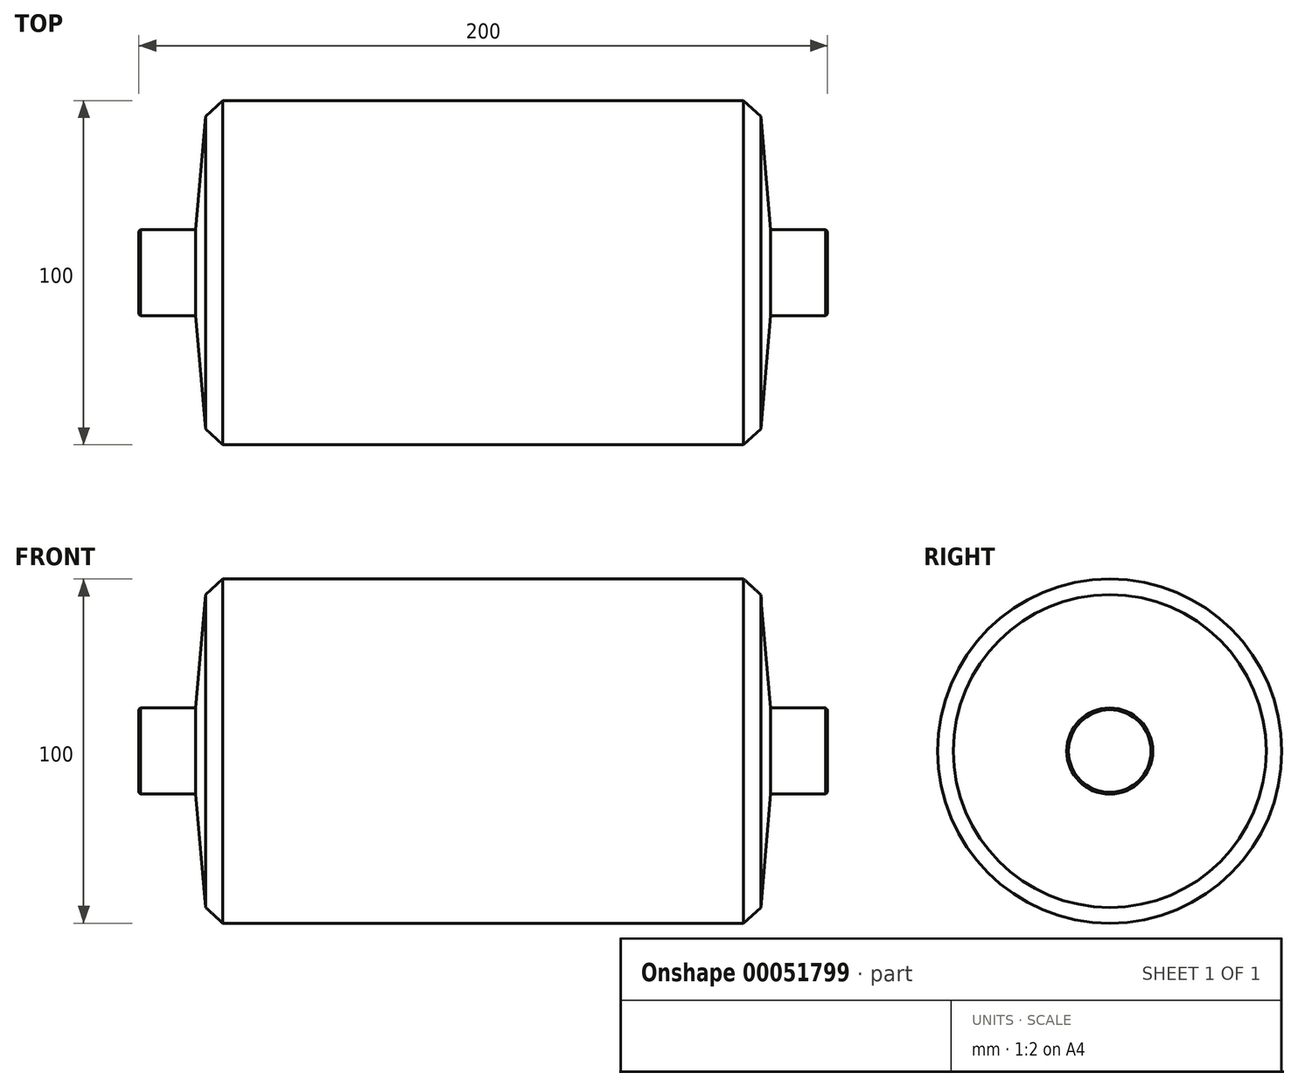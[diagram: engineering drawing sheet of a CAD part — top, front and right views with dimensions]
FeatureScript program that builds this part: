
annotation { "Feature Type Name" : "Feature", "Feature Type Description" : "" }
export const myFeature = defineFeature(function(context is Context, id is Id, definition is map)
    precondition{}
    {
        {
            var Q0;
            Q0=qCreatedBy(makeId("Top.planeOp"),FACE);
            var sketch = newSketch(context, id + "F0", { "sketchPlane" : qUnion([Q0])});
            skLineSegment(sketch, "E0", {"start": v(0, 0) * mm, "end": v(200, 0) * mm});
            skLineSegment(sketch, "E1", {"start": v(200, 0) * mm, "end": v(200, 12.5) * mm});
            skLineSegment(sketch, "E2", {"start": v(200, 12.5) * mm, "end": v(183.5, 12.5) * mm});
            skLineSegment(sketch, "E3", {"start": v(183.5, 12.5) * mm, "end": v(180.22, 50) * mm});
            skLineSegment(sketch, "E4", {"start": v(19.78, 50) * mm, "end": v(16.5, 12.5) * mm});
            skLineSegment(sketch, "E5", {"start": v(16.5, 12.5) * mm, "end": v(0, 12.5) * mm});
            skLineSegment(sketch, "E6", {"start": v(0, 12.5) * mm, "end": v(0, 0) * mm});
            skLineSegment(sketch, "E7", {"start": v(19.78, 50) * mm, "end": v(180.22, 50) * mm});
            skSolve(sketch);
        }
        {
            var Q0;
            Q0=makeQuery(id+"F0.imprint","IMPRINT",FACE,{"disambiguationData":[TD([[makeQuery(id+"F0.imprint","IMPRINT",EDGE,{"derivedFrom":sQuery(id+"F0.wireOp",EDGE,"E0")}),1.0]])]});
            var Q1;
            Q1=sQuery(id+"F0.wireOp",EDGE,"E0");
            revolve(context, id + "F1", {"entities" : qUnion([Q0]), "axis" : qUnion([Q1]), "revolveType" : RevolveType.FULL});
        }
        {
            var Q0;
            Q0=makeQuery(id+"F1.opRevolve","SWEPT_EDGE",EDGE,{"disambiguationData":[OSD([sQuery(id+"F0.wireOp",EDGE,"E4"),sQuery(id+"F0.wireOp",EDGE,"E7")])]});
            chamfer(context, id + "F2", {"entities" : qUnion([Q0]), "width" : 5 * mm, "tangentPropagation" : true});
        }
        {
            var Q0;
            Q0=makeQuery(id+"F1.opRevolve","SWEPT_EDGE",EDGE,{"disambiguationData":[OSD([sQuery(id+"F0.wireOp",EDGE,"E3"),sQuery(id+"F0.wireOp",EDGE,"E7")])]});
            chamfer(context, id + "F3", {"entities" : qUnion([Q0]), "width" : 5 * mm, "tangentPropagation" : true});
        }
        {
            var Q0;
            Q0=makeQuery(id+"F1.opRevolve","SWEPT_EDGE",EDGE,{"disambiguationData":[OSD([sQuery(id+"F0.wireOp",EDGE,"E5"),sQuery(id+"F0.wireOp",EDGE,"E6")])]});
            var Q1;
            Q1=makeQuery(id+"F1.opRevolve","SWEPT_EDGE",EDGE,{"disambiguationData":[OSD([sQuery(id+"F0.wireOp",EDGE,"E1"),sQuery(id+"F0.wireOp",EDGE,"E2")])]});
            chamfer(context, id + "F4", {"entities" : qUnion([Q0, Q1]), "chamferType" : ChamferType.OFFSET_ANGLE, "width" : .5 * mm, "oppositeDirection" : false, "angle" : 45 * degree, "tangentPropagation" : true});
        }
    });
